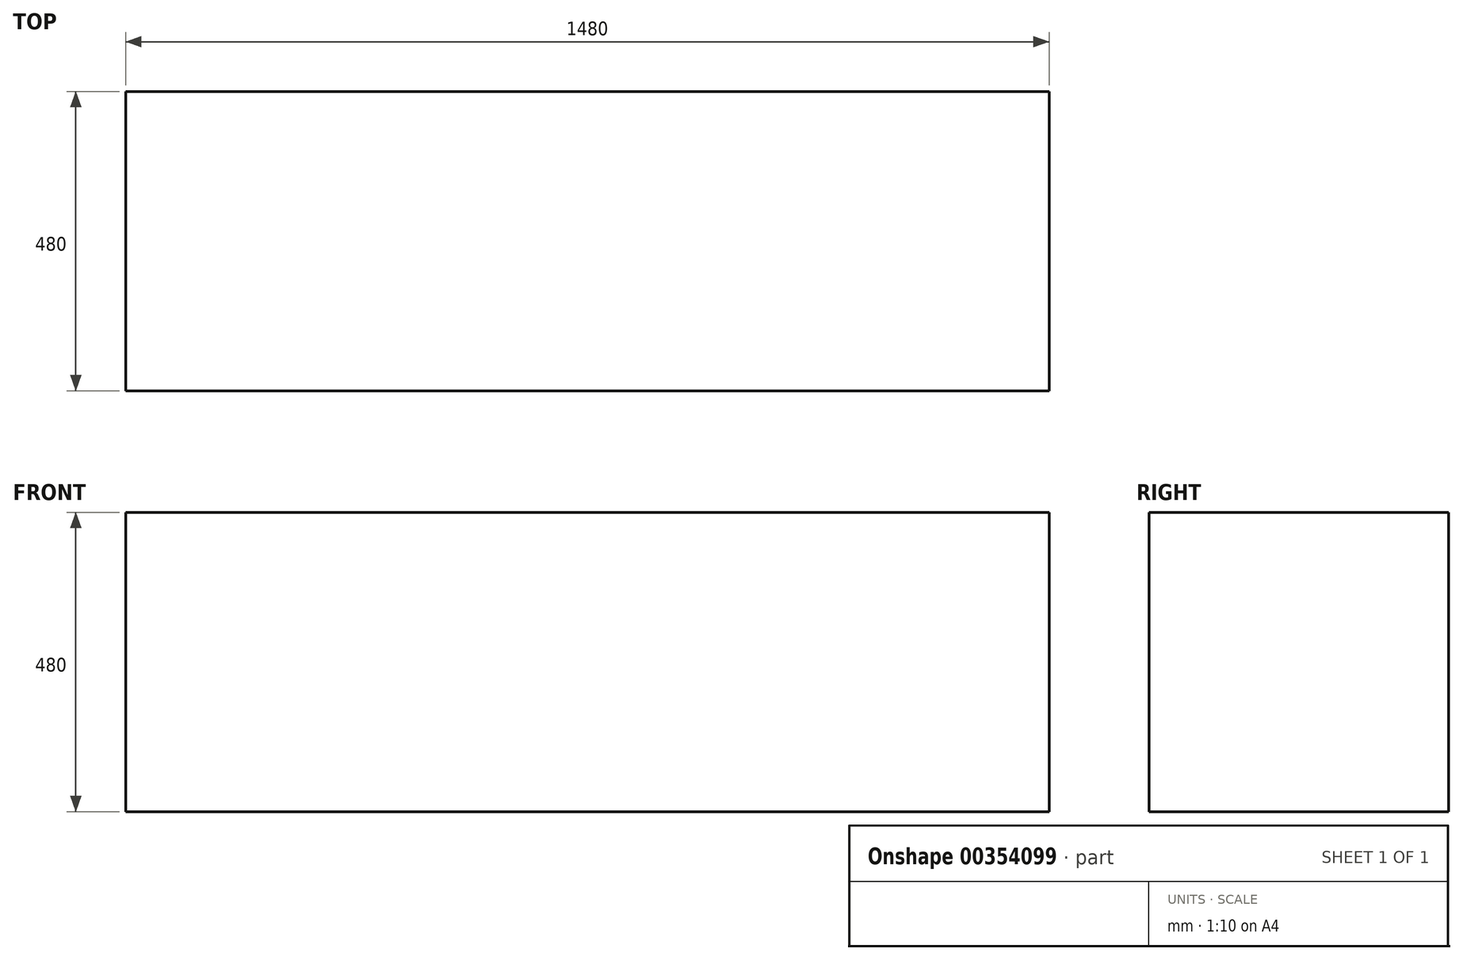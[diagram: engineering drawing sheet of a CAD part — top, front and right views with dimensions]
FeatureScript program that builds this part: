
annotation { "Feature Type Name" : "Feature", "Feature Type Description" : "" }
export const myFeature = defineFeature(function(context is Context, id is Id, definition is map)
    precondition{}
    {
        {
            var Q0;
            Q0=qCreatedBy(makeId("Top.planeOp"),FACE);
            var sketch = newSketch(context, id + "F0", { "sketchPlane" : qUnion([Q0])});
            skLineSegment(sketch, "E0.bottom", {"start": v(-769.4, 268.4) * mm, "end": v(710.6, 268.4) * mm});
            skLineSegment(sketch, "E0.top", {"start": v(-769.4, -211.6) * mm, "end": v(710.6, -211.6) * mm});
            skLineSegment(sketch, "E0.left", {"start": v(-769.4, 268.4) * mm, "end": v(-769.4, -211.6) * mm});
            skLineSegment(sketch, "E0.right", {"start": v(710.6, 268.4) * mm, "end": v(710.6, -211.6) * mm});
            skSolve(sketch);
        }
        {
            var Q0;
            Q0=makeQuery(id+"F0.imprint","IMPRINT",FACE,{"disambiguationData":[TD([[makeQuery(id+"F0.imprint","IMPRINT",EDGE,{"derivedFrom":sQuery(id+"F0.wireOp",EDGE,"E0.bottom")}),-1.0]])]});
            extrude(context, id + "F1", {"entities" : qUnion([Q0]), "depth" : 480 * mm});
        }
    });
